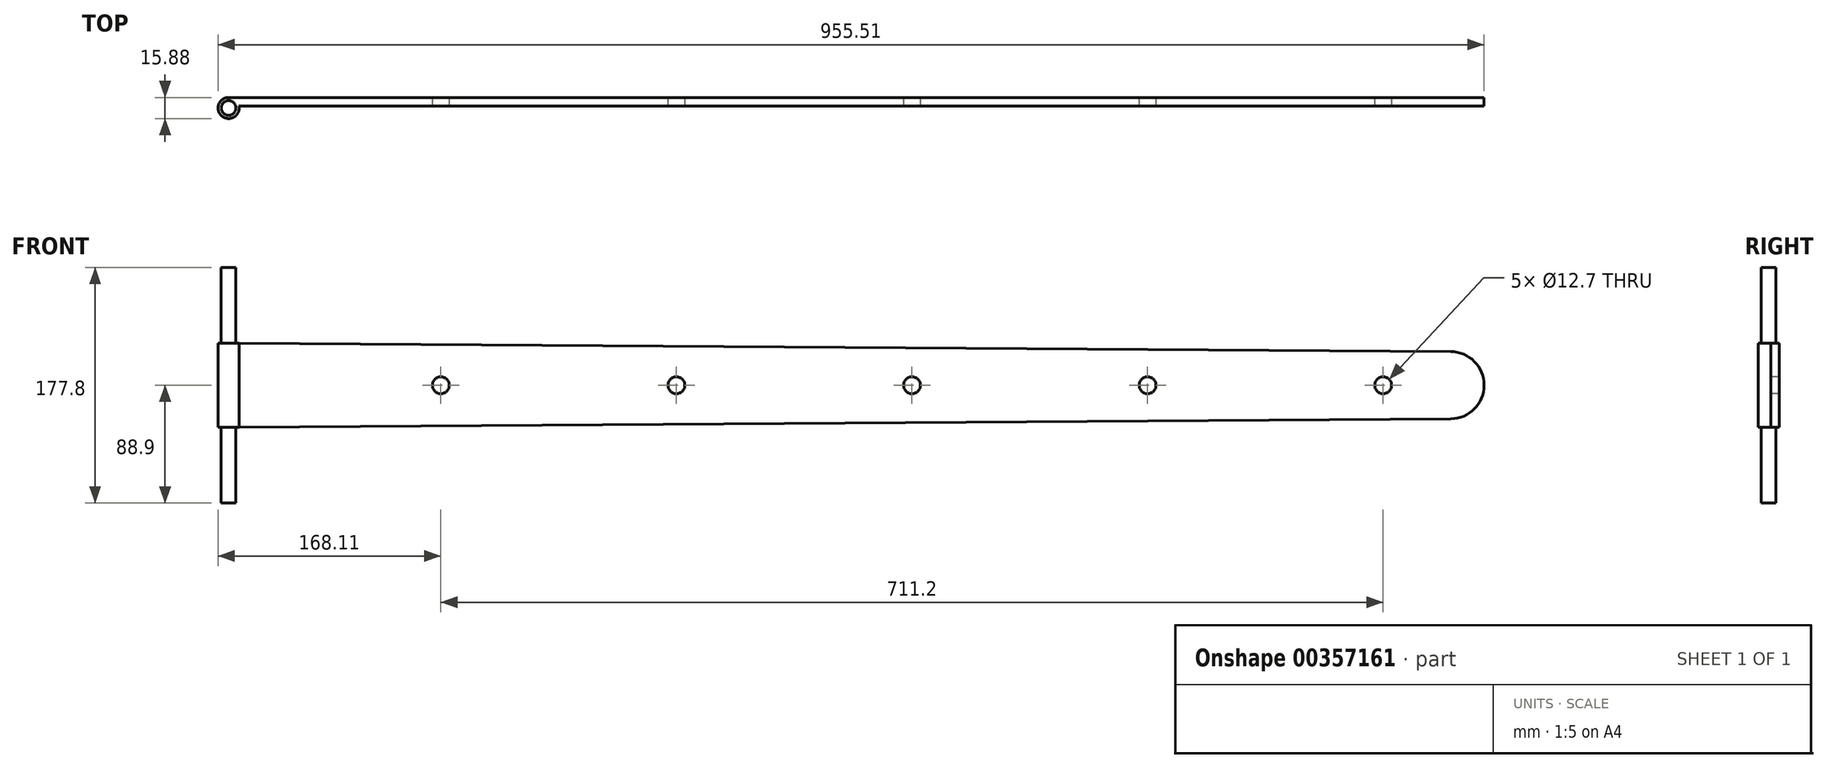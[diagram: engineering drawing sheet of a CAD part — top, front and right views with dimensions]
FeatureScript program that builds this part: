
annotation { "Feature Type Name" : "Feature", "Feature Type Description" : "" }
export const myFeature = defineFeature(function(context is Context, id is Id, definition is map)
    precondition{}
    {
        {
            var Q0;
            Q0=qCreatedBy(makeId("Front.planeOp"),FACE);
            var sketch = newSketch(context, id + "F0", { "sketchPlane" : qUnion([Q0])});
            skLineSegment(sketch, "E0", {"start": v(0, 63.5) * mm, "end": v(914.58, 57.15) * mm});
            skArc(sketch, "E1", {"start": v(914.58, 6.35) * mm, "mid": v(939.8, 31.75) * mm, "end": v(914.58, 57.15) * mm});
            skLineSegment(sketch, "E2", {"start": v(914.58, 6.35) * mm, "end": v(0, 0) * mm});
            skLineSegment(sketch, "E3", {"start": v(0, 63.5) * mm, "end": v(0, 0) * mm});
            skSolve(sketch);
        }
        {
            var Q0;
            Q0=makeQuery(id+"F0.imprint","IMPRINT",FACE,{"disambiguationData":[TD([[makeQuery(id+"F0.imprint","IMPRINT",EDGE,{"derivedFrom":sQuery(id+"F0.wireOp",EDGE,"E0")}),-1.0]])]});
            extrude(context, id + "F1", {"entities" : qUnion([Q0]), "depth" : 6.35 * mm});
        }
        {
            var Q0;
            Q0=qCreatedBy(makeId("Top.planeOp"),FACE);
            var sketch = newSketch(context, id + "F2", { "sketchPlane" : qUnion([Q0])});
            skArc(sketch, "E4", {"start": v(-7.78, 0) * mm, "mid": v(-12.8, -14.09) * mm, "end": v(0, -6.35) * mm});
            skLineSegment(sketch, "E5", {"start": v(0, 0) * mm, "end": v(-7.78, 0) * mm});
            skLineSegment(sketch, "E6", {"start": v(0, -6.35) * mm, "end": v(0, 0) * mm});
            skSolve(sketch);
        }
        {
            var Q0;
            Q0 = qSketchRegion(id + "F2", true);
            var Q1;
            Q1=makeQuery(id+"F1.opExtrude","SWEPT_FACE",FACE,{"disambiguationData":[OSD([sQuery(id+"F0.wireOp",EDGE,"E0")])]});
            extrude(context, id + "F3", {"entities" : qUnion([Q0]), "operationType" : NewBodyOperationType.ADD, "endBoundEntityFace" : qUnion([Q1]), "depth" : 63.5 * mm});
        }
        {
            var Q0;
            Q0=makeQuery(id+"F3.opExtrude","CAP_FACE",FACE,{"disambiguationData":[OSD([sQuery(id+"F2.wireOp",EDGE,"E4"),sQuery(id+"F2.wireOp",EDGE,"E5"),sQuery(id+"F2.wireOp",EDGE,"E6")])],"isStart":false});
            var Q1;
            Q1=makeQuery(id+"F3.opExtrude","CAP_FACE",FACE,{"disambiguationData":[OSD([sQuery(id+"F2.wireOp",EDGE,"E4"),sQuery(id+"F2.wireOp",EDGE,"E5"),sQuery(id+"F2.wireOp",EDGE,"E6")])],"isStart":true});
            cPlane(context, id + "F4", {"entities" : qUnion([Q0, Q1]), "cplaneType" : CPlaneType.MID_PLANE, "offset" : 25.4 * mm, "width" : 152.4 * mm, "height" : 152.4 * mm});
        }
        {
            var Q0;
            Q0=qCreatedBy(id+"F4.planeOp",FACE);
            var sketch = newSketch(context, id + "F5", { "sketchPlane" : qUnion([Q0])});
            skCircle(sketch, "E7", {"center": v(-7.78, -7.94) * mm, "radius": 5.56 * mm});
            skSolve(sketch);
        }
        {
            var Q0;
            Q0 = qSketchRegion(id + "F5", true);
            extrude(context, id + "F6", {"entities" : qUnion([Q0]), "operationType" : NewBodyOperationType.ADD, "depth" : 88.9 * mm, "hasSecondDirection" : true, "secondDirectionOppositeDirection" : true, "secondDirectionDepth" : 88.9 * mm});
        }
        {
            var Q0;
            Q0=makeQuery(id+"F1.opExtrude","CAP_FACE",FACE,{"disambiguationData":[OSD([sQuery(id+"F0.wireOp",EDGE,"E0"),sQuery(id+"F0.wireOp",EDGE,"E1"),sQuery(id+"F0.wireOp",EDGE,"E2"),sQuery(id+"F0.wireOp",EDGE,"E3")])],"isStart":false});
            var sketch = newSketch(context, id + "F7", { "sketchPlane" : qUnion([Q0])});
            skCircle(sketch, "E8", {"center": v(152.4, 31.75) * mm, "radius": 6.35 * mm});
            skCircle(sketch, "E9", {"center": v(330.2, 31.75) * mm, "radius": 6.35 * mm});
            skCircle(sketch, "E10", {"center": v(508, 31.75) * mm, "radius": 6.35 * mm});
            skCircle(sketch, "E11", {"center": v(685.8, 31.75) * mm, "radius": 6.35 * mm});
            skCircle(sketch, "E12", {"center": v(863.6, 31.75) * mm, "radius": 6.35 * mm});
            skLineSegment(sketch, "E13", {"start": v(633.28, 31.75) * mm, "end": v(914.4, 31.75) * mm, "construction": true});
            skSolve(sketch);
        }
        {
            var Q0;
            Q0 = qSketchRegion(id + "F7", true);
            extrude(context, id + "F8", {"entities" : qUnion([Q0]), "operationType" : NewBodyOperationType.REMOVE, "endBound" : BoundingType.UP_TO_NEXT, "oppositeDirection" : true, "depth" : 25.4 * mm});
        }
    });
